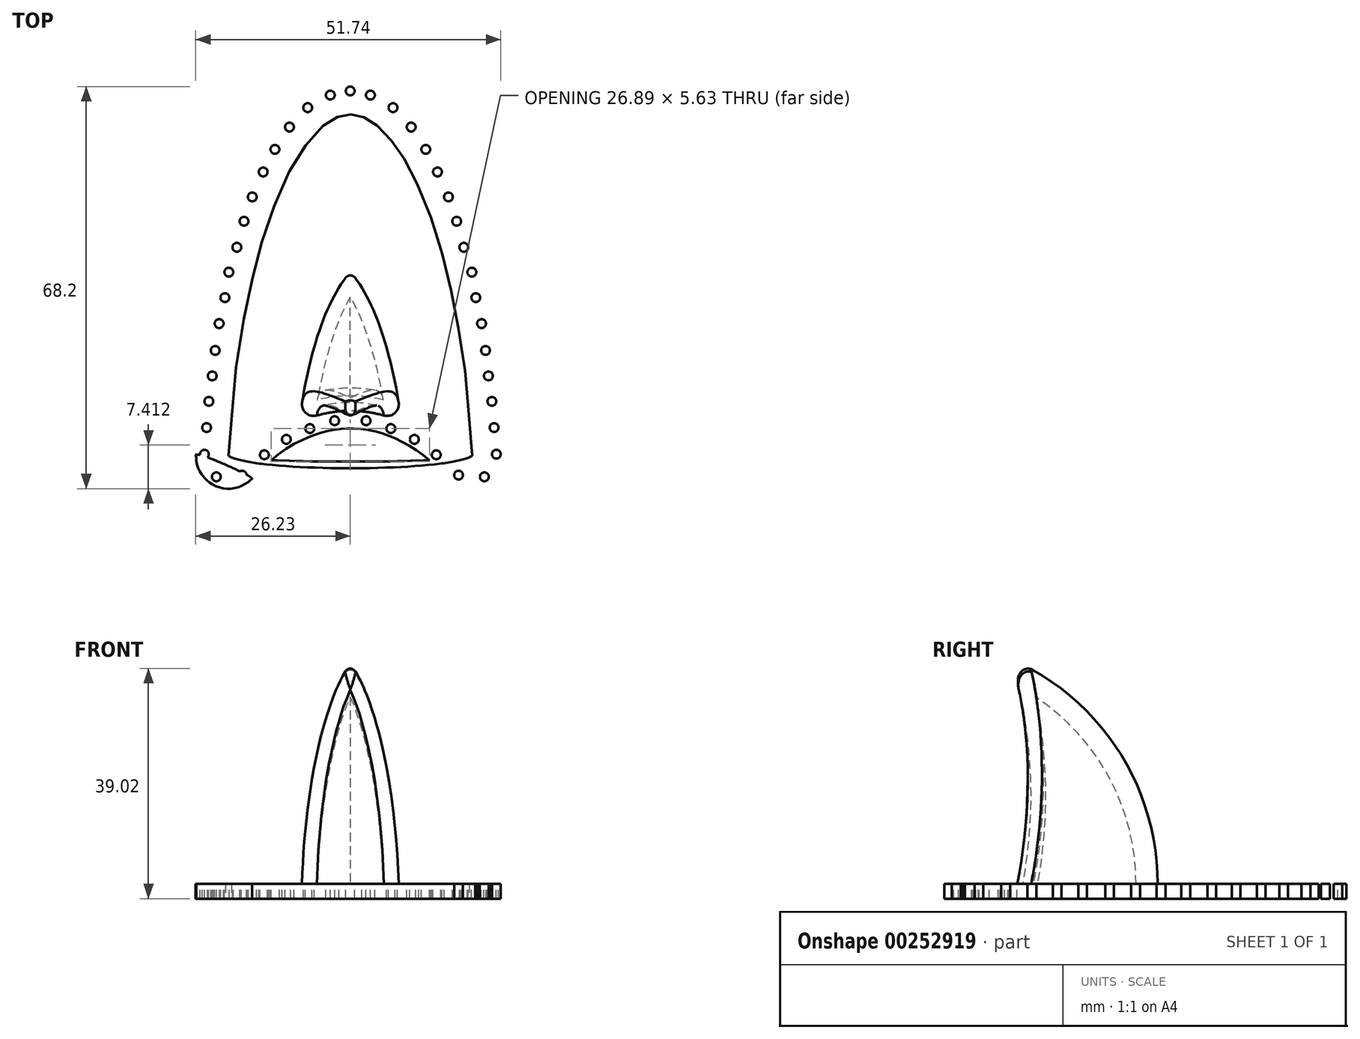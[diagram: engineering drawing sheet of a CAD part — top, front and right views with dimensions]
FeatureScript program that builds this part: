
annotation { "Feature Type Name" : "Feature", "Feature Type Description" : "" }
export const myFeature = defineFeature(function(context is Context, id is Id, definition is map)
    precondition{}
    {
        {
            var Q0;
            Q0=qCreatedBy(makeId("Top.planeOp"),FACE);
            var sketch = newSketch(context, id + "F0", { "sketchPlane" : qUnion([Q0])});
            skEllipticalArc(sketch, "E0", {});
            skLineSegment(sketch, "E1", {"start": v(-9.77, 0) * mm, "end": v(9.77, 0) * mm});
            skEllipticalArc(sketch, "E2.MirrorCS", {});
            skPoint(sketch, "E3.orphan", {"position": v(19.67, 0) * mm});
            skPoint(sketch, "E4.orphan", {"position": v(-19.67, 0) * mm});
            skArc(sketch, "E5", {"start": v(0.8, 41.28) * mm, "mid": v(0, 41.67) * mm, "end": v(-0.8, 41.28) * mm});
            const initialGuessF0  = {"E0": [-0.004951468965243606, 0, 0, 1, 0.04483062756087124, 0.01471736642922363, 4.71238898038469, 5.8823911117091585], "E2.MirrorCS": [0.004951468965243606, 0, 0, 1, 0.04483062756087124, 0.01471736642922363, 0.4007941954704271, 1.5707963267948966]};
            skSetInitialGuess(sketch, initialGuessF0);
            skSolve(sketch);
        }
        {
            var Q0;
            Q0=qCreatedBy(makeId("Top.planeOp"),FACE);
            var sketch = newSketch(context, id + "F1", { "sketchPlane" : qUnion([Q0])});
            skEllipticalArc(sketch, "E6", {});
            skLineSegment(sketch, "E7", {"start": v(-40.68, -140.7) * mm, "end": v(40.68, -140.7) * mm});
            const initialGuessF1  = {"E6": [0, -0.14069192111492157, 0, 1, 0.08080634676819629, 0.04068115038200901, 4.71238898038469, 1.5707963267948966]};
            skSetInitialGuess(sketch, initialGuessF1);
            skSolve(sketch);
        }
        {
            var Q0;
            Q0=makeQuery(id+"F0.imprint","IMPRINT",FACE,{"disambiguationData":[TD([[makeQuery(id+"F0.imprint","IMPRINT",EDGE,{"derivedFrom":sQuery(id+"F0.wireOp",EDGE,"E0")}),1.0]])]});
            var Q1;
            Q1=sQuery(id+"F0.wireOp",EDGE,"E1");
            revolve(context, id + "F2", {"entities" : qUnion([Q0]), "axis" : qUnion([Q1]), "revolveType" : RevolveType.ONE_DIRECTION, "angle" : 180 * degree});
        }
        {
            var Q0;
            Q0=makeQuery(id+"F1.imprint","IMPRINT",FACE,{"disambiguationData":[TD([[makeQuery(id+"F1.imprint","IMPRINT",EDGE,{"derivedFrom":sQuery(id+"F1.wireOp",EDGE,"E6")}),1.0]])]});
            var Q1;
            Q1=sQuery(id+"F1.wireOp",EDGE,"E7");
            revolve(context, id + "F3", {"entities" : qUnion([Q0]), "axis" : qUnion([Q1]), "revolveType" : RevolveType.FULL});
        }
        {
            var Q0;
            Q0=makeQuery(id+"F3.opRevolve","SWEPT_BODY",BODY,{"disambiguationData":[OSD([sQuery(id+"F1.wireOp",EDGE,"E6"),sQuery(id+"F1.wireOp",EDGE,"E7")])]});
            transform(context, id + "F4", {"entities" : qUnion([Q0]), "transformType" : TransformType.TRANSLATION_3D, "dx" : 0 * mm, "dy" : 80 * mm, "dz" : 15 * mm, "makeCopy" : false});
        }
        {
            var Q0;
            Q0=makeQuery(id+"F3.opRevolve","SWEPT_BODY",BODY,{"disambiguationData":[OSD([sQuery(id+"F1.wireOp",EDGE,"E6"),sQuery(id+"F1.wireOp",EDGE,"E7")])]});
            var Q1;
            Q1=makeQuery(id+"F2.opRevolve","SWEPT_BODY",BODY,{"disambiguationData":[OSD([sQuery(id+"F0.wireOp",EDGE,"E0"),sQuery(id+"F0.wireOp",EDGE,"E1")])]});
            booleanBodies(context, id + "F5", {"operationType" : BooleanOperationType.SUBTRACTION, "tools" : qUnion([Q0]), "targets" : qUnion([Q1])});
        }
        {
            var Q0;
            Q0=makeQuery(id+"F5.opBoolean","INTERSECT",EDGE,{"derivedFrom":[makeQuery(id+"F2.opRevolve","SWEPT_FACE",FACE,{"disambiguationData":[OSD([sQuery(id+"F0.wireOp",EDGE,"E0")])]}),makeQuery(id+"F3.opRevolve","SWEPT_FACE",FACE,{"disambiguationData":[OSD([sQuery(id+"F1.wireOp",EDGE,"E6")])]})]});
            fillet(context, id + "F6", {"entities" : qUnion([Q0]), "radius" : 2 * mm, "tangentPropagation" : true, "allowEdgeOverflow" : false});
        }
        {
            var Q0;
            Q0=makeQuery(id+"F2.opRevolve","CAP_FACE",FACE,{"disambiguationData":[OSD([sQuery(id+"F0.wireOp",EDGE,"E0"),sQuery(id+"F0.wireOp",EDGE,"E1")])],"isStart":false});
            shell(context, id + "F7", {"entities" : qUnion([Q0]), "thickness" : 2.5 * mm});
        }
        {
            var Q0;
            Q0=qCreatedBy(makeId("Top.planeOp"),FACE);
            var sketch = newSketch(context, id + "F8", { "sketchPlane" : qUnion([Q0])});
            skFitSpline(sketch, "E8.0", {"points": [v(1.4, 72.89) * mm, v(0, 73) * mm, v(-1.4, 72.89) * mm, v(-2.76, 72.57) * mm, v(-4.1, 72.07) * mm, v(-5.82, 71.15) * mm, v(-7.87, 69.57) * mm, v(-10.18, 67.05) * mm, v(-12.35, 63.92) * mm, v(-14.38, 60.2) * mm, v(-15.97, 56.64) * mm, v(-17.16, 53.5) * mm, v(-18.02, 51.01) * mm, v(-18.84, 48.4) * mm, v(-19.86, 44.79) * mm, v(-21.02, 40.02) * mm, v(-22.2, 33.96) * mm, v(-23.2, 27.59) * mm, v(-23.97, 20.97) * mm, v(-24.44, 15.27) * mm, v(-24.7, 10.63) * mm, v(-24.85, 7.12) * mm, v(-24.94, 3.57) * mm, v(-24.97, 0) * mm, v(-24.94, -3.57) * mm, v(-24.85, -7.12) * mm, v(-24.7, -10.63) * mm, v(-24.44, -15.27) * mm, v(-23.97, -20.97) * mm, v(-23.2, -27.59) * mm, v(-22.2, -33.96) * mm, v(-21.02, -40.02) * mm, v(-19.86, -44.79) * mm, v(-18.84, -48.4) * mm, v(-18.02, -51.01) * mm, v(-17.16, -53.5) * mm, v(-15.97, -56.64) * mm, v(-14.38, -60.2) * mm, v(-12.35, -63.92) * mm, v(-10.18, -67.05) * mm, v(-7.87, -69.57) * mm, v(-5.82, -71.15) * mm, v(-4.1, -72.07) * mm, v(-2.76, -72.57) * mm, v(-1.4, -72.89) * mm, v(0, -73) * mm, v(1.4, -72.89) * mm, v(2.76, -72.57) * mm, v(4.1, -72.07) * mm, v(5.82, -71.15) * mm, v(7.87, -69.57) * mm, v(10.18, -67.05) * mm, v(12.35, -63.92) * mm, v(14.38, -60.2) * mm, v(15.97, -56.64) * mm, v(17.16, -53.5) * mm, v(18.02, -51.01) * mm, v(18.84, -48.4) * mm, v(19.86, -44.79) * mm, v(21.02, -40.02) * mm, v(22.2, -33.96) * mm, v(23.2, -27.59) * mm, v(23.97, -20.97) * mm, v(24.44, -15.27) * mm, v(24.7, -10.63) * mm, v(24.85, -7.12) * mm, v(24.94, -3.57) * mm, v(24.97, 0) * mm, v(24.94, 3.57) * mm, v(24.85, 7.12) * mm, v(24.7, 10.63) * mm, v(24.44, 15.27) * mm, v(23.97, 20.97) * mm, v(23.2, 27.59) * mm, v(22.2, 33.96) * mm, v(21.02, 40.02) * mm, v(19.86, 44.79) * mm, v(18.84, 48.4) * mm, v(18.02, 51.01) * mm, v(17.16, 53.5) * mm, v(15.97, 56.64) * mm, v(14.38, 60.2) * mm, v(12.35, 63.92) * mm, v(10.18, 67.05) * mm, v(7.87, 69.57) * mm, v(5.82, 71.15) * mm, v(4.1, 72.07) * mm, v(2.76, 72.57) * mm, v(1.4, 72.89) * mm, v(0, 73) * mm, v(-1.4, 72.89) * mm], "construction": true});
            skFitSpline(sketch, "E9.0", {"points": [v(24.67, 11.29) * mm, v(24.68, 11.09) * mm, v(24.67, 10.79) * mm, v(24.62, 10.39) * mm, v(24.53, 9.99) * mm, v(24.38, 9.52) * mm, v(24.1, 8.96) * mm, v(23.82, 8.56) * mm, v(23.55, 8.25) * mm, v(23.33, 8.03) * mm, v(23.1, 7.84) * mm, v(22.85, 7.66) * mm, v(22.58, 7.5) * mm, v(22.3, 7.37) * mm, v(22.02, 7.25) * mm, v(21.73, 7.16) * mm, v(21.43, 7.08) * mm, v(21.12, 7.04) * mm, v(20.81, 7.02) * mm, v(20.4, 7.02) * mm, v(19.9, 7.08) * mm, v(19.39, 7.22) * mm, v(19.01, 7.38) * mm, v(18.74, 7.52) * mm, v(18.48, 7.68) * mm, v(18.15, 7.92) * mm, v(17.92, 8.13) * mm, v(17.78, 8.28) * mm], "construction": true});
            skFitSpline(sketch, "E10.0", {"points": [v(22.5, 2.35) * mm, v(21.82, 3.34) * mm, v(20.42, 5.27) * mm, v(18.13, 7.97) * mm, v(16.07, 10.04) * mm, v(14.3, 11.57) * mm, v(12.91, 12.64) * mm, v(11.45, 13.65) * mm, v(9.94, 14.54) * mm, v(8.4, 15.32) * mm, v(7.06, 15.88) * mm, v(5.97, 16.26) * mm, v(4.85, 16.6) * mm, v(3.46, 16.91) * mm, v(1.77, 17.15) * mm, v(0.36, 17.22) * mm, v(-0.78, 17.2) * mm, v(-1.64, 17.14) * mm, v(-2.5, 17.05) * mm, v(-3.63, 16.87) * mm, v(-5.03, 16.55) * mm, v(-6.4, 16.12) * mm, v(-7.48, 15.7) * mm, v(-8.55, 15.24) * mm, v(-9.85, 14.6) * mm, v(-11.35, 13.7) * mm, v(-12.8, 12.72) * mm, v(-14.2, 11.65) * mm, v(-15.54, 10.5) * mm, v(-16.84, 9.26) * mm, v(-18.48, 7.55) * mm, v(-20.4, 5.28) * mm, v(-21.82, 3.34) * mm, v(-22.5, 2.35) * mm], "construction": true});
            skFitSpline(sketch, "E11.0", {"points": [v(-17.69, 8.37) * mm, v(-17.7, 8.36) * mm, v(-17.72, 8.33) * mm, v(-17.75, 8.3) * mm, v(-17.78, 8.28) * mm, v(-17.8, 8.26) * mm, v(-17.83, 8.23) * mm, v(-17.87, 8.18) * mm, v(-17.95, 8.1) * mm, v(-18.04, 8.02) * mm, v(-18.2, 7.89) * mm, v(-18.4, 7.73) * mm, v(-18.75, 7.5) * mm, v(-19.12, 7.33) * mm, v(-19.5, 7.19) * mm, v(-19.82, 7.1) * mm, v(-20.12, 7.05) * mm, v(-20.43, 7.02) * mm, v(-20.74, 7.01) * mm, v(-21.17, 7.04) * mm, v(-21.67, 7.13) * mm, v(-22.27, 7.34) * mm, v(-22.8, 7.62) * mm, v(-23.23, 7.94) * mm, v(-23.52, 8.22) * mm, v(-23.73, 8.45) * mm, v(-23.92, 8.7) * mm, v(-24.14, 9.04) * mm, v(-24.37, 9.5) * mm, v(-24.56, 10.07) * mm, v(-24.67, 10.68) * mm, v(-24.68, 11.08) * mm, v(-24.67, 11.29) * mm], "construction": true});
            skCircle(sketch, "E12", {"center": v(24.38, 15.86) * mm, "radius": 0.75 * mm});
            skCircle(sketch, "E13", {"center": v(24, 20.3) * mm, "radius": 0.75 * mm});
            skCircle(sketch, "E14", {"center": v(23.42, 24.62) * mm, "radius": 0.75 * mm});
            skCircle(sketch, "E15", {"center": v(22.93, 28.94) * mm, "radius": 0.75 * mm});
            skCircle(sketch, "E16", {"center": v(22.25, 33.5) * mm, "radius": 0.75 * mm});
            skCircle(sketch, "E17", {"center": v(21.29, 37.9) * mm, "radius": 0.75 * mm});
            skCircle(sketch, "E18", {"center": v(20.6, 42.22) * mm, "radius": 0.75 * mm});
            skCircle(sketch, "E19", {"center": v(19.25, 46.44) * mm, "radius": 0.75 * mm});
            skCircle(sketch, "E20", {"center": v(18.04, 50.85) * mm, "radius": 0.75 * mm});
            skCircle(sketch, "E21", {"center": v(16.63, 54.97) * mm, "radius": 0.75 * mm});
            skCircle(sketch, "E22", {"center": v(24.76, 11.34) * mm, "radius": 0.75 * mm});
            skCircle(sketch, "E23", {"center": v(22.72, 7.51) * mm, "radius": 0.75 * mm});
            skCircle(sketch, "E24", {"center": v(18.36, 7.8) * mm, "radius": 0.75 * mm});
            skCircle(sketch, "E25", {"center": v(14.58, 11.24) * mm, "radius": 0.75 * mm});
            skCircle(sketch, "E26", {"center": v(10.85, 13.86) * mm, "radius": 0.75 * mm});
            skCircle(sketch, "E27", {"center": v(6.87, 15.7) * mm, "radius": 0.75 * mm});
            skCircle(sketch, "E28", {"center": v(2.66, 17.02) * mm, "radius": 0.75 * mm});
            skCircle(sketch, "E29", {"center": v(14.78, 59.2) * mm, "radius": 0.75 * mm});
            skCircle(sketch, "E30", {"center": v(12.8, 63.04) * mm, "radius": 0.75 * mm});
            skCircle(sketch, "E31", {"center": v(10.32, 66.82) * mm, "radius": 0.75 * mm});
            skCircle(sketch, "E32", {"center": v(7.23, 70.12) * mm, "radius": 0.75 * mm});
            skCircle(sketch, "E33", {"center": v(3.4, 72.25) * mm, "radius": 0.75 * mm});
            skCircle(sketch, "E34.MirrorC", {"center": v(-2.66, 17.02) * mm, "radius": 0.75 * mm});
            skCircle(sketch, "E35.MirrorC", {"center": v(-6.87, 15.7) * mm, "radius": 0.75 * mm});
            skCircle(sketch, "E36.MirrorC", {"center": v(-10.85, 13.86) * mm, "radius": 0.75 * mm});
            skCircle(sketch, "E37.MirrorC", {"center": v(-14.58, 11.24) * mm, "radius": 0.75 * mm});
            skCircle(sketch, "E38.MirrorC", {"center": v(-18.36, 7.8) * mm, "radius": 0.75 * mm});
            skCircle(sketch, "E39.MirrorC", {"center": v(-22.72, 7.51) * mm, "radius": 0.75 * mm});
            skCircle(sketch, "E40.MirrorC", {"center": v(-24.76, 11.34) * mm, "radius": 0.75 * mm});
            skCircle(sketch, "E41.MirrorC", {"center": v(-24.38, 15.86) * mm, "radius": 0.75 * mm});
            skCircle(sketch, "E42.MirrorC", {"center": v(-24, 20.3) * mm, "radius": 0.75 * mm});
            skCircle(sketch, "E43.MirrorC", {"center": v(-23.42, 24.62) * mm, "radius": 0.75 * mm});
            skCircle(sketch, "E44.MirrorC", {"center": v(-22.93, 28.94) * mm, "radius": 0.75 * mm});
            skCircle(sketch, "E45.MirrorC", {"center": v(-22.25, 33.5) * mm, "radius": 0.75 * mm});
            skCircle(sketch, "E46.MirrorC", {"center": v(-21.29, 37.9) * mm, "radius": 0.75 * mm});
            skCircle(sketch, "E47.MirrorC", {"center": v(-20.6, 42.22) * mm, "radius": 0.75 * mm});
            skCircle(sketch, "E48.MirrorC", {"center": v(-19.25, 46.44) * mm, "radius": 0.75 * mm});
            skCircle(sketch, "E49.MirrorC", {"center": v(-18.04, 50.85) * mm, "radius": 0.75 * mm});
            skCircle(sketch, "E50.MirrorC", {"center": v(-16.63, 54.97) * mm, "radius": 0.75 * mm});
            skCircle(sketch, "E51.MirrorC", {"center": v(-14.78, 59.2) * mm, "radius": 0.75 * mm});
            skCircle(sketch, "E52.MirrorC", {"center": v(-12.8, 63.04) * mm, "radius": 0.75 * mm});
            skCircle(sketch, "E53.MirrorC", {"center": v(-10.32, 66.82) * mm, "radius": 0.75 * mm});
            skCircle(sketch, "E54.MirrorC", {"center": v(-7.23, 70.12) * mm, "radius": 0.75 * mm});
            skCircle(sketch, "E55.MirrorC", {"center": v(-3.4, 72.25) * mm, "radius": 0.75 * mm});
            skCircle(sketch, "E56", {"center": v(-0.02, 72.94) * mm, "radius": 0.75 * mm});
            skFitSpline(sketch, "E57.0", {"points": [v(1.62, 74.37) * mm, v(0, 74.5) * mm, v(-1.62, 74.37) * mm, v(-3.72, 73.9) * mm, v(-6.2, 72.75) * mm, v(-8.9, 70.67) * mm, v(-11.36, 67.98) * mm, v(-13.63, 64.7) * mm, v(-15.73, 60.87) * mm, v(-17.35, 57.21) * mm, v(-18.57, 54.02) * mm, v(-19.45, 51.48) * mm, v(-20.27, 48.83) * mm, v(-21.3, 45.16) * mm, v(-22.48, 40.34) * mm, v(-23.68, 34.22) * mm, v(-24.68, 27.8) * mm, v(-25.47, 21.11) * mm, v(-26.03, 14.23) * mm, v(-26.32, 8.35) * mm, v(-26.44, 3.6) * mm, v(-26.47, 0) * mm, v(-26.44, -3.6) * mm, v(-26.32, -8.35) * mm, v(-26.03, -14.23) * mm, v(-25.47, -21.11) * mm, v(-24.68, -27.8) * mm, v(-23.68, -34.22) * mm, v(-22.48, -40.34) * mm, v(-21.3, -45.16) * mm, v(-20.27, -48.83) * mm, v(-19.45, -51.48) * mm, v(-18.57, -54.02) * mm, v(-17.35, -57.21) * mm, v(-15.73, -60.87) * mm, v(-13.63, -64.7) * mm, v(-11.36, -67.98) * mm, v(-8.9, -70.67) * mm, v(-6.2, -72.75) * mm, v(-3.72, -73.9) * mm, v(-1.62, -74.37) * mm, v(0, -74.5) * mm, v(1.62, -74.37) * mm, v(3.72, -73.9) * mm, v(6.2, -72.75) * mm, v(8.9, -70.67) * mm, v(11.36, -67.98) * mm, v(13.63, -64.7) * mm, v(15.73, -60.87) * mm, v(17.35, -57.21) * mm, v(18.57, -54.02) * mm, v(19.45, -51.48) * mm, v(20.27, -48.83) * mm, v(21.3, -45.16) * mm, v(22.48, -40.34) * mm, v(23.68, -34.22) * mm, v(24.68, -27.8) * mm, v(25.47, -21.11) * mm, v(26.03, -14.23) * mm, v(26.32, -8.35) * mm, v(26.44, -3.6) * mm, v(26.47, 0) * mm, v(26.44, 3.6) * mm, v(26.32, 8.35) * mm, v(26.03, 14.23) * mm, v(25.47, 21.11) * mm, v(24.68, 27.8) * mm, v(23.68, 34.22) * mm, v(22.48, 40.34) * mm, v(21.3, 45.16) * mm, v(20.27, 48.83) * mm, v(19.45, 51.48) * mm, v(18.57, 54.02) * mm, v(17.35, 57.21) * mm, v(15.73, 60.87) * mm, v(13.63, 64.7) * mm, v(11.36, 67.98) * mm, v(8.9, 70.67) * mm, v(6.2, 72.75) * mm, v(3.72, 73.9) * mm, v(1.62, 74.37) * mm, v(0, 74.5) * mm, v(-1.62, 74.37) * mm]});
            skFitSpline(sketch, "E58.0", {"points": [v(-16.69, 7.25) * mm, v(-16.88, 7.05) * mm, v(-17.29, 6.67) * mm, v(-18, 6.2) * mm, v(-18.76, 5.84) * mm, v(-19.59, 5.6) * mm, v(-20.42, 5.5) * mm, v(-21.3, 5.53) * mm, v(-22.12, 5.69) * mm, v(-22.93, 5.98) * mm, v(-23.67, 6.39) * mm, v(-24.23, 6.82) * mm, v(-24.63, 7.2) * mm, v(-24.91, 7.52) * mm, v(-25.16, 7.86) * mm, v(-25.46, 8.32) * mm, v(-25.77, 8.94) * mm, v(-26.03, 9.72) * mm, v(-26.17, 10.54) * mm, v(-26.18, 11.09) * mm, v(-26.16, 11.37) * mm, v(-16.69, 7.25) * mm]});
            skFitSpline(sketch, "E59.0", {"points": [v(21.26, 1.5) * mm, v(20.6, 2.47) * mm, v(19.24, 4.34) * mm, v(17.03, 6.95) * mm, v(15.04, 8.94) * mm, v(13.35, 10.4) * mm, v(12.02, 11.43) * mm, v(10.64, 12.38) * mm, v(9.22, 13.23) * mm, v(7.76, 13.96) * mm, v(6.52, 14.48) * mm, v(5.5, 14.83) * mm, v(4.47, 15.14) * mm, v(3.18, 15.44) * mm, v(1.63, 15.66) * mm, v(0.33, 15.72) * mm, v(-0.72, 15.7) * mm, v(-1.51, 15.65) * mm, v(-2.3, 15.56) * mm, v(-3.35, 15.4) * mm, v(-4.63, 15.1) * mm, v(-5.9, 14.7) * mm, v(-6.91, 14.31) * mm, v(-7.91, 13.88) * mm, v(-9.62, 13.03) * mm, v(-11.48, 11.85) * mm, v(-13.25, 10.49) * mm, v(-14.54, 9.38) * mm, v(-15.78, 8.2) * mm, v(-17.36, 6.55) * mm, v(-19.22, 4.35) * mm, v(-20.6, 2.47) * mm, v(-21.26, 1.5) * mm]});
            skFitSpline(sketch, "E60.0", {"points": [v(26.16, 11.37) * mm, v(26.18, 11.1) * mm, v(26.17, 10.54) * mm, v(26.03, 9.73) * mm, v(25.78, 8.95) * mm, v(25.4, 8.2) * mm, v(24.93, 7.52) * mm, v(24.44, 7) * mm, v(24.01, 6.65) * mm, v(23.67, 6.4) * mm, v(23.3, 6.19) * mm, v(22.93, 6) * mm, v(22.54, 5.84) * mm, v(22.13, 5.7) * mm, v(21.71, 5.61) * mm, v(21.15, 5.52) * mm, v(20.43, 5.5) * mm, v(19.6, 5.6) * mm, v(18.76, 5.84) * mm, v(18.13, 6.14) * mm, v(17.64, 6.43) * mm, v(17.19, 6.76) * mm, v(16.88, 7.04) * mm, v(16.69, 7.25) * mm]});
            skFitSpline(sketch, "E61.0", {"points": [v(20.67, 11.08) * mm, v(20.53, 13.77) * mm, v(20.15, 19.14) * mm, v(19.39, 25.83) * mm, v(18.6, 31.16) * mm, v(17.9, 35.13) * mm, v(17.1, 39.07) * mm, v(16.19, 42.98) * mm, v(15.14, 46.86) * mm, v(13.93, 50.7) * mm, v(12.54, 54.48) * mm, v(11.17, 57.59) * mm, v(9.94, 60) * mm, v(9.1, 61.46) * mm, v(8.37, 62.6) * mm, v(7.6, 63.72) * mm, v(6.78, 64.8) * mm, v(5.88, 65.8) * mm, v(5.15, 66.52) * mm, v(4.38, 67.2) * mm, v(3.7, 67.69) * mm, v(3.12, 68.04) * mm, v(2.67, 68.29) * mm, v(2.2, 68.5) * mm, v(1.73, 68.68) * mm, v(1.24, 68.82) * mm, v(0.74, 68.91) * mm, v(0.23, 68.96) * mm, v(-0.28, 68.96) * mm, v(-0.78, 68.9) * mm, v(-1.28, 68.8) * mm, v(-1.78, 68.66) * mm, v(-2.4, 68.42) * mm, v(-3, 68.12) * mm, v(-3.6, 67.75) * mm, v(-4.42, 67.17) * mm, v(-5.56, 66.17) * mm, v(-6.91, 64.64) * mm, v(-8.1, 63.02) * mm, v(-9.54, 60.76) * mm, v(-11.1, 57.8) * mm, v(-12.69, 54.1) * mm, v(-14.05, 50.33) * mm, v(-15.23, 46.52) * mm, v(-16.26, 42.68) * mm, v(-17.16, 38.8) * mm, v(-18.2, 33.6) * mm, v(-19.25, 27.04) * mm, v(-20.15, 19.07) * mm, v(-20.53, 13.75) * mm, v(-20.67, 11.08) * mm, v(20.67, 11.08) * mm]});
            skFitSpline(sketch, "E62.0", {"points": [v(20.67, 11.08) * mm, v(20, 11.8) * mm, v(18.6, 13.2) * mm, v(16.36, 15.1) * mm, v(13.99, 16.84) * mm, v(11.88, 18.1) * mm, v(10.09, 18.98) * mm, v(8.26, 19.76) * mm, v(6.4, 20.38) * mm, v(4.47, 20.83) * mm, v(3.25, 21.03) * mm, v(2.25, 21.14) * mm, v(1.26, 21.23) * mm, v(-0.46, 21.29) * mm, v(-2.43, 21.16) * mm, v(-4.38, 20.84) * mm, v(-5.84, 20.51) * mm, v(-7.27, 20.1) * mm, v(-9.13, 19.42) * mm, v(-10.92, 18.6) * mm, v(-12.66, 17.63) * mm, v(-14.35, 16.57) * mm, v(-16.34, 15.13) * mm, v(-18.59, 13.2) * mm, v(-19.99, 11.8) * mm, v(-20.67, 11.08) * mm, v(20.67, 11.08) * mm]});
            skSolve(sketch);
        }
        {
            var Q0;
            Q0 = qSketchRegion(id + "F8", true);
            extrude(context, id + "F9", {"entities" : qUnion([Q0]), "oppositeDirection" : true, "depth" : 2.5 * mm});
        }
    });
